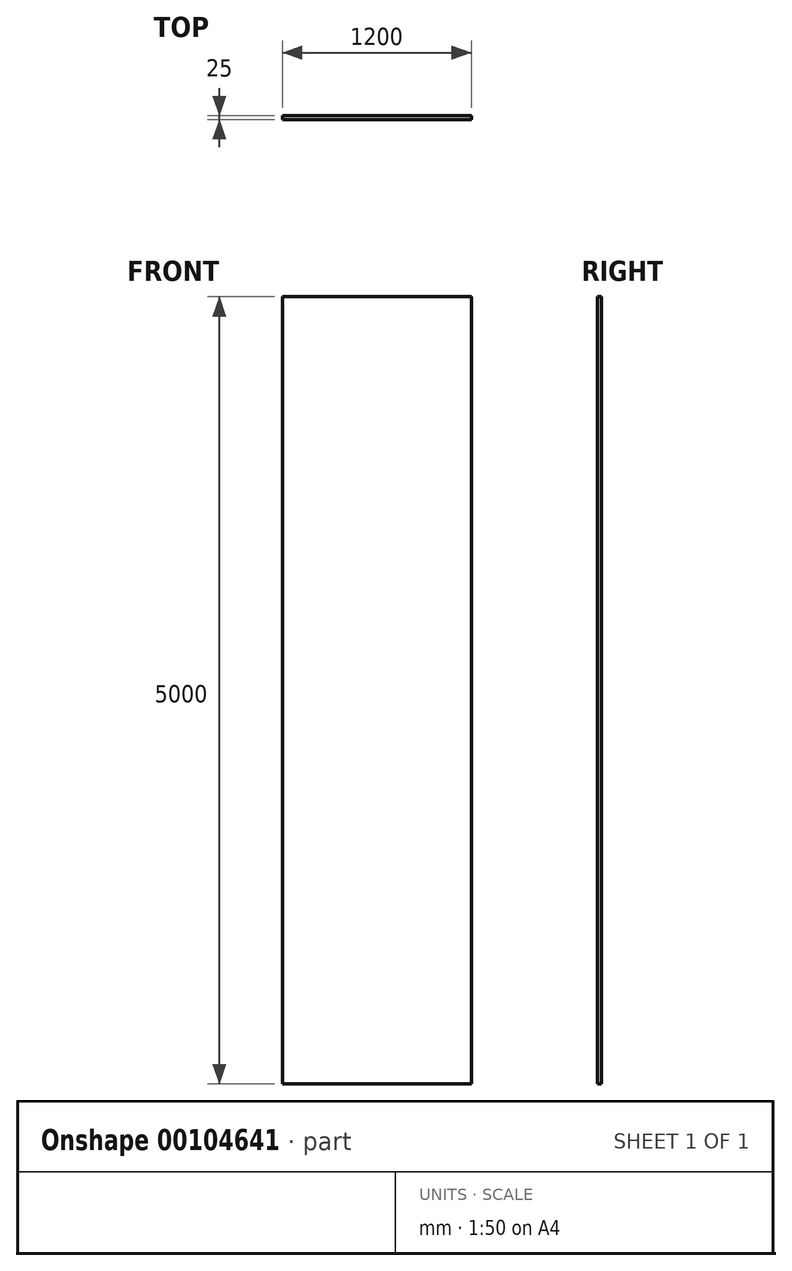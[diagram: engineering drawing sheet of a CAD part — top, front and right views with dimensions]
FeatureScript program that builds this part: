
annotation { "Feature Type Name" : "Feature", "Feature Type Description" : "" }
export const myFeature = defineFeature(function(context is Context, id is Id, definition is map)
    precondition{}
    {
        {
            var Q0;
            Q0=qCreatedBy(makeId("Front.planeOp"),FACE);
            var sketch = newSketch(context, id + "F0", { "sketchPlane" : qUnion([Q0])});
            skLineSegment(sketch, "E0.bottom", {"start": v(0, 0) * mm, "end": v(1200, 0) * mm});
            skLineSegment(sketch, "E0.top", {"start": v(0, -5000) * mm, "end": v(1200, -5000) * mm});
            skLineSegment(sketch, "E0.left", {"start": v(0, 0) * mm, "end": v(0, -5000) * mm});
            skLineSegment(sketch, "E0.right", {"start": v(1200, 0) * mm, "end": v(1200, -5000) * mm});
            skSolve(sketch);
        }
        {
            var Q0;
            Q0=makeQuery(id+"F0.imprint","IMPRINT",FACE,{"disambiguationData":[TD([[makeQuery(id+"F0.imprint","IMPRINT",EDGE,{"derivedFrom":sQuery(id+"F0.wireOp",EDGE,"E0.bottom")}),-1.0]])]});
            extrude(context, id + "F1", {"entities" : qUnion([Q0]), "depth" : 25 * mm});
        }
    });
